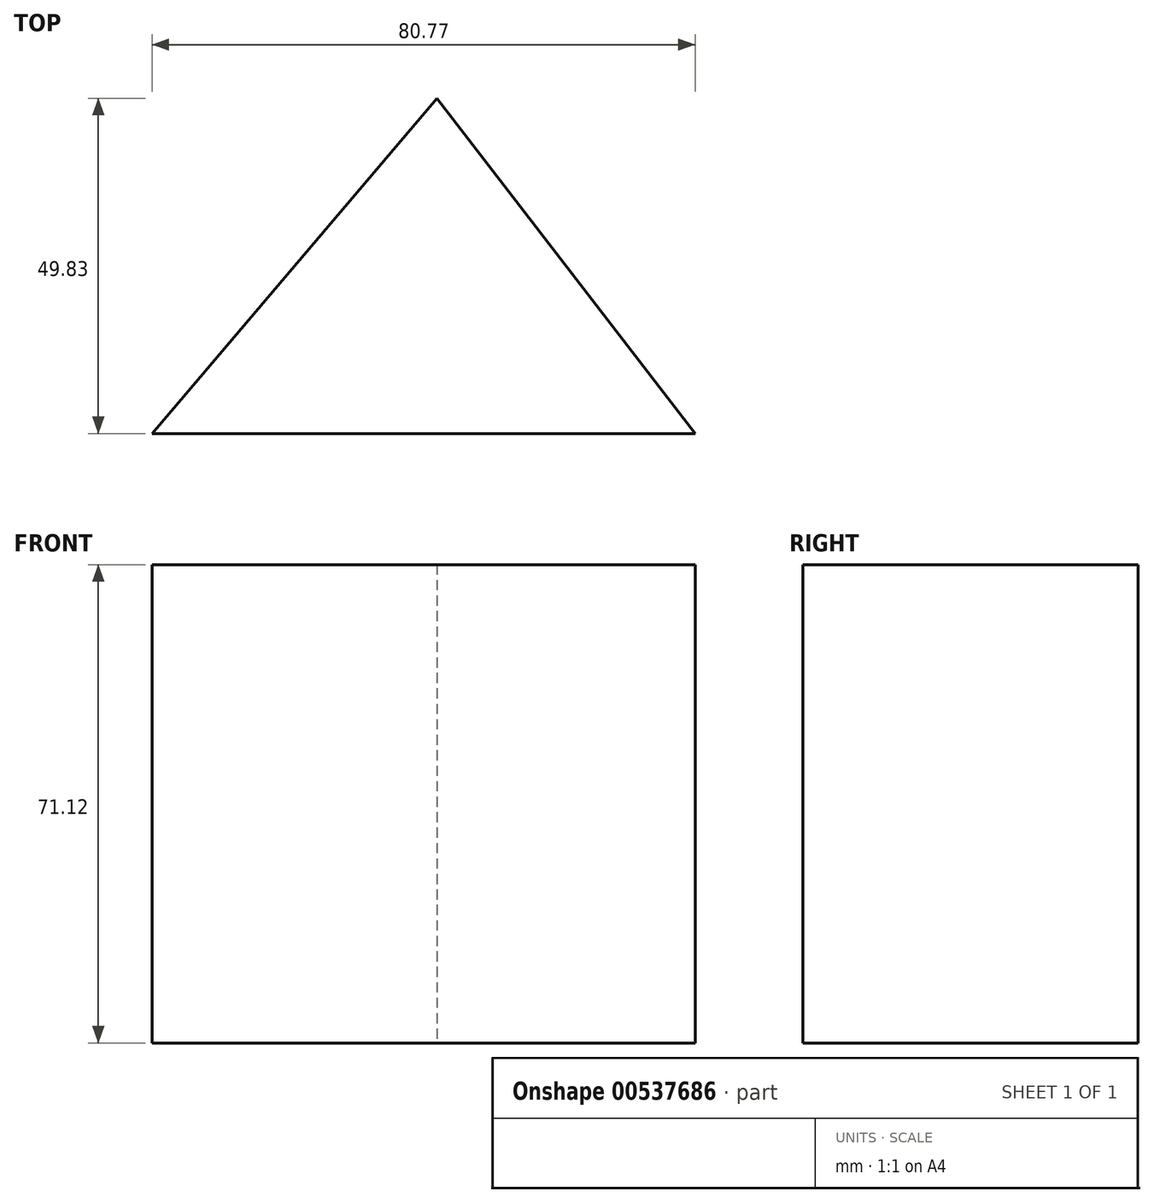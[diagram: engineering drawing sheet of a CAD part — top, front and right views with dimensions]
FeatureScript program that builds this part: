
annotation { "Feature Type Name" : "Feature", "Feature Type Description" : "" }
export const myFeature = defineFeature(function(context is Context, id is Id, definition is map)
    precondition{}
    {
        {
            var Q0;
            Q0=qCreatedBy(makeId("Top.planeOp"),FACE);
            var sketch = newSketch(context, id + "F0", { "sketchPlane" : qUnion([Q0])});
            skLineSegment(sketch, "E0", {"start": v(0, 49.83) * mm, "end": v(-42.37, 0) * mm});
            skLineSegment(sketch, "E1", {"start": v(-42.37, 0) * mm, "end": v(38.4, 0) * mm});
            skLineSegment(sketch, "E2", {"start": v(38.4, 0) * mm, "end": v(0, 49.83) * mm});
            skSolve(sketch);
        }
        {
            var Q0;
            Q0=makeQuery(id+"F0.imprint","IMPRINT",FACE,{"disambiguationData":[TD([[makeQuery(id+"F0.imprint","IMPRINT",EDGE,{"derivedFrom":sQuery(id+"F0.wireOp",EDGE,"E0")}),1.0]])]});
            extrude(context, id + "F1", {"entities" : qUnion([Q0]), "depth" : 71.12 * mm, "offsetDistance" : 25.4 * mm});
        }
    });
